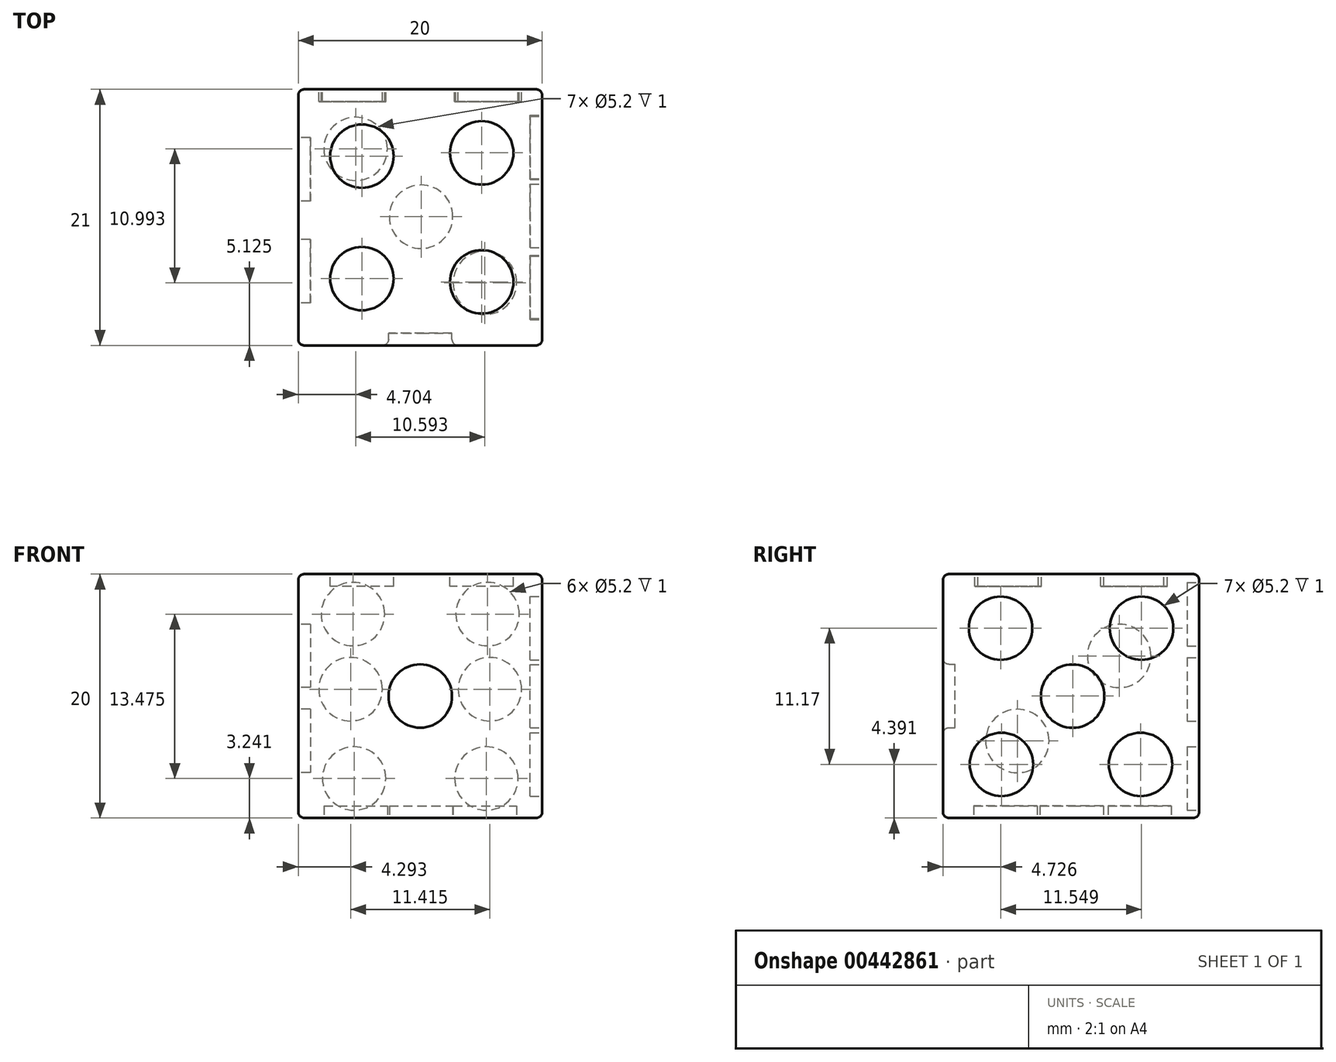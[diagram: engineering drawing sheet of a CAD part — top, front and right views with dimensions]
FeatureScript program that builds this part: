
annotation { "Feature Type Name" : "Feature", "Feature Type Description" : "" }
export const myFeature = defineFeature(function(context is Context, id is Id, definition is map)
    precondition{}
    {
        {
            var Q0;
            Q0=qCreatedBy(makeId("Front.planeOp"),FACE);
            var sketch = newSketch(context, id + "F0", { "sketchPlane" : qUnion([Q0])});
            skLineSegment(sketch, "E0.bottom", {"start": v(0, 0) * mm, "end": v(20, 0) * mm});
            skLineSegment(sketch, "E0.top", {"start": v(0, 20) * mm, "end": v(20, 20) * mm});
            skLineSegment(sketch, "E0.left", {"start": v(0, 0) * mm, "end": v(0, 20) * mm});
            skLineSegment(sketch, "E0.right", {"start": v(20, 0) * mm, "end": v(20, 20) * mm});
            skSolve(sketch);
        }
        {
            var Q0;
            Q0 = qSketchRegion(id + "F0", true);
            extrude(context, id + "F1", {"entities" : qUnion([Q0]), "depth" : 20 * mm});
        }
        {
            var Q0;
            Q0=makeQuery(id+"F1.opExtrude","CAP_FACE",FACE,{"disambiguationData":[OSD([sQuery(id+"F0.wireOp",EDGE,"E0.bottom"),sQuery(id+"F0.wireOp",EDGE,"E0.top"),sQuery(id+"F0.wireOp",EDGE,"E0.left"),sQuery(id+"F0.wireOp",EDGE,"E0.right")])],"isStart":false});
            var sketch = newSketch(context, id + "F2", { "sketchPlane" : qUnion([Q0])});
            skLineSegment(sketch, "E1", {"start": v(0, 20) * mm, "end": v(20, 0) * mm, "construction": true});
            skLineSegment(sketch, "E2", {"start": v(20, 0) * mm, "end": v(20, 20) * mm, "construction": true});
            skLineSegment(sketch, "E3", {"start": v(20, 20) * mm, "end": v(0, 0) * mm, "construction": true});
            skCircle(sketch, "E4", {"center": v(10, 10) * mm, "radius": 2.6 * mm});
            skSolve(sketch);
        }
        {
            var Q0;
            Q0=makeQuery(id+"F2.imprint","IMPRINT",FACE,{"disambiguationData":[TD([[makeQuery(id+"F2.imprint","IMPRINT",EDGE,{"derivedFrom":sQuery(id+"F2.wireOp",EDGE,"E4")}),-1.0]])]});
            extrude(context, id + "F3", {"entities" : qUnion([Q0]), "operationType" : NewBodyOperationType.ADD, "depth" : 1 * mm});
        }
        {
            var Q0;
            {var subQ0=sQuery(id+"F0.wireOp",EDGE,"E0.left");Q0=makeQuery(id+"F3.boolean.opBoolean","MERGE",FACE,{"derivedFrom":[makeQuery(id+"F1.opExtrude","SWEPT_FACE",FACE,{"disambiguationData":[OSD([subQ0])]}),makeQuery(id+"F3.opExtrude","SWEPT_FACE",FACE,{"disambiguationData":[OSD([subQ0])]})]});}
            var sketch = newSketch(context, id + "F4", { "sketchPlane" : qUnion([Q0])});
            skCircle(sketch, "E5", {"center": v(6.56, 13.3) * mm, "radius": 2.6 * mm});
            skCircle(sketch, "E6", {"center": v(14.9, 6.31) * mm, "radius": 2.6 * mm});
            skSolve(sketch);
        }
        {
            var Q0;
            Q0=makeQuery(id+"F4.imprint","IMPRINT",FACE,{"disambiguationData":[TD([[makeQuery(id+"F4.imprint","IMPRINT",EDGE,{"derivedFrom":sQuery(id+"F4.wireOp",EDGE,"E5")}),1.0]])]});
            var Q1;
            Q1=makeQuery(id+"F4.imprint","IMPRINT",FACE,{"disambiguationData":[TD([[makeQuery(id+"F4.imprint","IMPRINT",EDGE,{"derivedFrom":sQuery(id+"F4.wireOp",EDGE,"E6")}),1.0]])]});
            extrude(context, id + "F5", {"entities" : qUnion([Q0, Q1]), "operationType" : NewBodyOperationType.REMOVE, "oppositeDirection" : true, "depth" : 1 * mm});
        }
        {
            var Q0;
            {var subQ0=sQuery(id+"F0.wireOp",EDGE,"E0.top");Q0=makeQuery(id+"F3.boolean.opBoolean","MERGE",FACE,{"derivedFrom":[makeQuery(id+"F1.opExtrude","SWEPT_FACE",FACE,{"disambiguationData":[OSD([subQ0])]}),makeQuery(id+"F3.opExtrude","SWEPT_FACE",FACE,{"disambiguationData":[OSD([subQ0])]})]});}
            var sketch = newSketch(context, id + "F6", { "sketchPlane" : qUnion([Q0])});
            skLineSegment(sketch, "E7", {"start": v(0, 0) * mm, "end": v(20, -21) * mm, "construction": true});
            skLineSegment(sketch, "E8", {"start": v(20, -21) * mm, "end": v(20, 0) * mm, "construction": true});
            skLineSegment(sketch, "E9", {"start": v(20, 0) * mm, "end": v(0, -21) * mm, "construction": true});
            skLineSegment(sketch, "E10", {"start": v(0, -21) * mm, "end": v(0, -10.5) * mm, "construction": true});
            skLineSegment(sketch, "E11", {"start": v(0, -10.5) * mm, "end": v(20, -10.5) * mm, "construction": true});
            skLineSegment(sketch, "E12", {"start": v(20, -10.5) * mm, "end": v(20, 0) * mm, "construction": true});
            skLineSegment(sketch, "E13", {"start": v(10, 0) * mm, "end": v(10, -21) * mm, "construction": true});
            skCircle(sketch, "E14", {"center": v(5.22, -5.48) * mm, "radius": 2.6 * mm});
            skCircle(sketch, "E15", {"center": v(15.04, -5.2) * mm, "radius": 2.6 * mm});
            skCircle(sketch, "E16.MirrorC", {"center": v(5.22, -15.52) * mm, "radius": 2.6 * mm});
            skCircle(sketch, "E17.MirrorC", {"center": v(15.04, -15.8) * mm, "radius": 2.6 * mm});
            skSolve(sketch);
        }
        {
            var Q0;
            Q0 = qSketchRegion(id + "F6", true);
            extrude(context, id + "F7", {"entities" : qUnion([Q0]), "operationType" : NewBodyOperationType.REMOVE, "oppositeDirection" : true, "depth" : 1 * mm});
        }
        {
            var Q0;
            {var subQ0=sQuery(id+"F0.wireOp",EDGE,"E0.bottom");Q0=makeQuery(id+"F3.boolean.opBoolean","MERGE",FACE,{"derivedFrom":[makeQuery(id+"F1.opExtrude","SWEPT_FACE",FACE,{"disambiguationData":[OSD([subQ0])]}),makeQuery(id+"F3.opExtrude","SWEPT_FACE",FACE,{"disambiguationData":[OSD([subQ0])]})]});}
            var sketch = newSketch(context, id + "F8", { "sketchPlane" : qUnion([Q0])});
            skCircle(sketch, "E18", {"center": v(15.52, 16.46) * mm, "radius": 3.34 * mm});
            skSolve(sketch);
        }
        {
            var Q0;
            Q0=makeQuery(id+"F8.imprint","IMPRINT",FACE,{"disambiguationData":[TD([[makeQuery(id+"F8.imprint","IMPRINT",EDGE,{"derivedFrom":sQuery(id+"F8.wireOp",EDGE,"E18")}),-1.0]])]});
            var sketch = newSketch(context, id + "F9", { "sketchPlane" : qUnion([Q0])});
            skLineSegment(sketch, "E19", {"start": v(0, 0) * mm, "end": v(20.13, 20.9) * mm, "construction": true});
            skCircle(sketch, "E20", {"center": v(4.7, 4.88) * mm, "radius": 2.6 * mm});
            skCircle(sketch, "E21", {"center": v(10.07, 10.45) * mm, "radius": 2.6 * mm});
            skCircle(sketch, "E22", {"center": v(15.3, 15.87) * mm, "radius": 2.6 * mm});
            skSolve(sketch);
        }
        {
            var Q0;
            Q0 = qSketchRegion(id + "F9", true);
            extrude(context, id + "F10", {"entities" : qUnion([Q0]), "operationType" : NewBodyOperationType.REMOVE, "oppositeDirection" : true, "depth" : 1 * mm});
        }
        {
            var Q0;
            Q0=makeQuery(id+"F1.opExtrude","CAP_FACE",FACE,{"disambiguationData":[OSD([sQuery(id+"F0.wireOp",EDGE,"E0.bottom"),sQuery(id+"F0.wireOp",EDGE,"E0.top"),sQuery(id+"F0.wireOp",EDGE,"E0.left"),sQuery(id+"F0.wireOp",EDGE,"E0.right")])],"isStart":true});
            var sketch = newSketch(context, id + "F11", { "sketchPlane" : qUnion([Q0])});
            skLineSegment(sketch, "E23", {"start": v(-10, 0) * mm, "end": v(-10, 20) * mm, "construction": true});
            skLineSegment(sketch, "E24", {"start": v(-20, 14.6) * mm, "end": v(0, 14.6) * mm, "construction": true});
            skLineSegment(sketch, "E25", {"start": v(-20, 3.72) * mm, "end": v(-20, 6.9) * mm, "construction": true});
            skLineSegment(sketch, "E26", {"start": v(-20, 6.9) * mm, "end": v(0, 6.9) * mm, "construction": true});
            skCircle(sketch, "E27", {"center": v(-15.42, 3.24) * mm, "radius": 2.6 * mm});
            skCircle(sketch, "E28", {"center": v(-15.7, 10.56) * mm, "radius": 2.6 * mm});
            skCircle(sketch, "E29", {"center": v(-15.51, 16.72) * mm, "radius": 2.6 * mm});
            skCircle(sketch, "E30.MirrorC", {"center": v(-4.49, 16.72) * mm, "radius": 2.6 * mm});
            skCircle(sketch, "E31.MirrorC", {"center": v(-4.3, 10.56) * mm, "radius": 2.6 * mm});
            skCircle(sketch, "E32.MirrorC", {"center": v(-4.58, 3.24) * mm, "radius": 2.6 * mm});
            skSolve(sketch);
        }
        {
            var Q0;
            Q0 = qSketchRegion(id + "F11", true);
            extrude(context, id + "F12", {"entities" : qUnion([Q0]), "operationType" : NewBodyOperationType.REMOVE, "oppositeDirection" : true, "depth" : 1 * mm});
        }
        {
            var Q0;
            {var subQ0=sQuery(id+"F0.wireOp",EDGE,"E0.right");Q0=makeQuery(id+"F3.boolean.opBoolean","MERGE",FACE,{"derivedFrom":[makeQuery(id+"F1.opExtrude","SWEPT_FACE",FACE,{"disambiguationData":[OSD([subQ0])]}),makeQuery(id+"F3.opExtrude","SWEPT_FACE",FACE,{"disambiguationData":[OSD([subQ0])]})]});}
            var sketch = newSketch(context, id + "F13", { "sketchPlane" : qUnion([Q0])});
            skLineSegment(sketch, "E33", {"start": v(0, 0) * mm, "end": v(-21, 20) * mm, "construction": true});
            skLineSegment(sketch, "E34", {"start": v(-21, 20) * mm, "end": v(0, 20) * mm, "construction": true});
            skLineSegment(sketch, "E35", {"start": v(0, 20) * mm, "end": v(-21, 0) * mm, "construction": true});
            skLineSegment(sketch, "E36", {"start": v(-21, 0) * mm, "end": v(-21, 10) * mm, "construction": true});
            skLineSegment(sketch, "E37", {"start": v(-21, 10) * mm, "end": v(0, 10) * mm, "construction": true});
            skLineSegment(sketch, "E38", {"start": v(0, 10) * mm, "end": v(0, 18.6) * mm, "construction": true});
            skLineSegment(sketch, "E39", {"start": v(0, 18.6) * mm, "end": v(0, 20) * mm, "construction": true});
            skLineSegment(sketch, "E40", {"start": v(-10.5, 20) * mm, "end": v(-10.5, 0) * mm, "construction": true});
            skCircle(sketch, "E41", {"center": v(-10.5, 10) * mm, "radius": 2.6 * mm});
            skCircle(sketch, "E42", {"center": v(-16.06, 15.3) * mm, "radius": 2.6 * mm});
            skCircle(sketch, "E43", {"center": v(-5.6, 14.67) * mm, "radius": 2.6 * mm});
            skCircle(sketch, "E44.MirrorC", {"center": v(-16.06, 4.7) * mm, "radius": 2.6 * mm});
            skCircle(sketch, "E45.MirrorC", {"center": v(-5.6, 5.33) * mm, "radius": 2.6 * mm});
            skSolve(sketch);
        }
        {
            var Q0;
            Q0=makeQuery(id+"F13.imprint","IMPRINT",FACE,{"disambiguationData":[TD([[makeQuery(id+"F13.imprint","IMPRINT",EDGE,{"derivedFrom":sQuery(id+"F13.wireOp",EDGE,"E41")}),-1.0]])]});
            var sketch = newSketch(context, id + "F14", { "sketchPlane" : qUnion([Q0])});
            skCircle(sketch, "E46", {"center": v(-16.2, 4.4) * mm, "radius": 2.6 * mm});
            skCircle(sketch, "E47", {"center": v(-10.37, 10) * mm, "radius": 2.6 * mm});
            skCircle(sketch, "E48", {"center": v(-16.27, 15.56) * mm, "radius": 2.6 * mm});
            skCircle(sketch, "E49.MirrorC", {"center": v(-4.73, 15.56) * mm, "radius": 2.6 * mm});
            skCircle(sketch, "E50.MirrorC", {"center": v(-4.8, 4.4) * mm, "radius": 2.6 * mm});
            skSolve(sketch);
        }
        {
            var Q0;
            Q0 = qSketchRegion(id + "F14", true);
            extrude(context, id + "F15", {"entities" : qUnion([Q0]), "operationType" : NewBodyOperationType.REMOVE, "oppositeDirection" : true, "depth" : 1 * mm});
        }
        {
            var Q0;
            Q0=makeQuery(id+"F3.opExtrude","CAP_EDGE",EDGE,{"disambiguationData":[OSD([sQuery(id+"F0.wireOp",EDGE,"E0.bottom")])],"isStart":false});
            var Q1;
            Q1=makeQuery(id+"F3.opExtrude","CAP_EDGE",EDGE,{"disambiguationData":[OSD([sQuery(id+"F0.wireOp",EDGE,"E0.right")])],"isStart":false});
            var Q2;
            {var subQ0=sQuery(id+"F0.wireOp",EDGE,"E0.right");var subQ1=sQuery(id+"F0.wireOp",EDGE,"E0.bottom");Q2=makeQuery(id+"F3.boolean.opBoolean","MERGE",EDGE,{"derivedFrom":[makeQuery(id+"F1.opExtrude","SWEPT_EDGE",EDGE,{"disambiguationData":[OSD([subQ1,subQ0])]}),makeQuery(id+"F3.opExtrude","SWEPT_EDGE",EDGE,{"disambiguationData":[OSD([subQ1,subQ0])]})]});}
            var Q3;
            Q3=makeQuery(id+"F1.opExtrude","CAP_EDGE",EDGE,{"disambiguationData":[OSD([sQuery(id+"F0.wireOp",EDGE,"E0.right")])],"isStart":true});
            var Q4;
            Q4=makeQuery(id+"F1.opExtrude","CAP_EDGE",EDGE,{"disambiguationData":[OSD([sQuery(id+"F0.wireOp",EDGE,"E0.bottom")])],"isStart":true});
            var Q5;
            {var subQ0=sQuery(id+"F0.wireOp",EDGE,"E0.right");var subQ1=sQuery(id+"F0.wireOp",EDGE,"E0.top");Q5=makeQuery(id+"F3.boolean.opBoolean","MERGE",EDGE,{"derivedFrom":[makeQuery(id+"F1.opExtrude","SWEPT_EDGE",EDGE,{"disambiguationData":[OSD([subQ1,subQ0])]}),makeQuery(id+"F3.opExtrude","SWEPT_EDGE",EDGE,{"disambiguationData":[OSD([subQ1,subQ0])]})]});}
            var Q6;
            Q6=makeQuery(id+"F3.opExtrude","CAP_EDGE",EDGE,{"disambiguationData":[OSD([sQuery(id+"F2.wireOp",EDGE,"E4")])],"isStart":false});
            var Q7;
            Q7=makeQuery(id+"F3.opExtrude","CAP_EDGE",EDGE,{"disambiguationData":[OSD([sQuery(id+"F0.wireOp",EDGE,"E0.top")])],"isStart":false});
            var Q8;
            {var subQ0=sQuery(id+"F0.wireOp",EDGE,"E0.left");var subQ1=sQuery(id+"F0.wireOp",EDGE,"E0.top");Q8=makeQuery(id+"F3.boolean.opBoolean","MERGE",EDGE,{"derivedFrom":[makeQuery(id+"F1.opExtrude","SWEPT_EDGE",EDGE,{"disambiguationData":[OSD([subQ1,subQ0])]}),makeQuery(id+"F3.opExtrude","SWEPT_EDGE",EDGE,{"disambiguationData":[OSD([subQ1,subQ0])]})]});}
            var Q9;
            Q9=makeQuery(id+"F1.opExtrude","CAP_EDGE",EDGE,{"disambiguationData":[OSD([sQuery(id+"F0.wireOp",EDGE,"E0.top")])],"isStart":true});
            var Q10;
            Q10=makeQuery(id+"F1.opExtrude","CAP_EDGE",EDGE,{"disambiguationData":[OSD([sQuery(id+"F0.wireOp",EDGE,"E0.left")])],"isStart":true});
            var Q11;
            Q11=makeQuery(id+"F3.opExtrude","CAP_EDGE",EDGE,{"disambiguationData":[OSD([sQuery(id+"F0.wireOp",EDGE,"E0.left")])],"isStart":false});
            var Q12;
            {var subQ0=sQuery(id+"F0.wireOp",EDGE,"E0.left");var subQ1=sQuery(id+"F0.wireOp",EDGE,"E0.bottom");Q12=makeQuery(id+"F3.boolean.opBoolean","MERGE",EDGE,{"derivedFrom":[makeQuery(id+"F1.opExtrude","SWEPT_EDGE",EDGE,{"disambiguationData":[OSD([subQ1,subQ0])]}),makeQuery(id+"F3.opExtrude","SWEPT_EDGE",EDGE,{"disambiguationData":[OSD([subQ1,subQ0])]})]});}
            fillet(context, id + "F16", {"entities" : qUnion([Q0, Q1, Q2, Q3, Q4, Q5, Q6, Q7, Q8, Q9, Q10, Q11, Q12]), "radius" : 0.5 * mm, "tangentPropagation" : true, "allowEdgeOverflow" : false});
        }
    });
